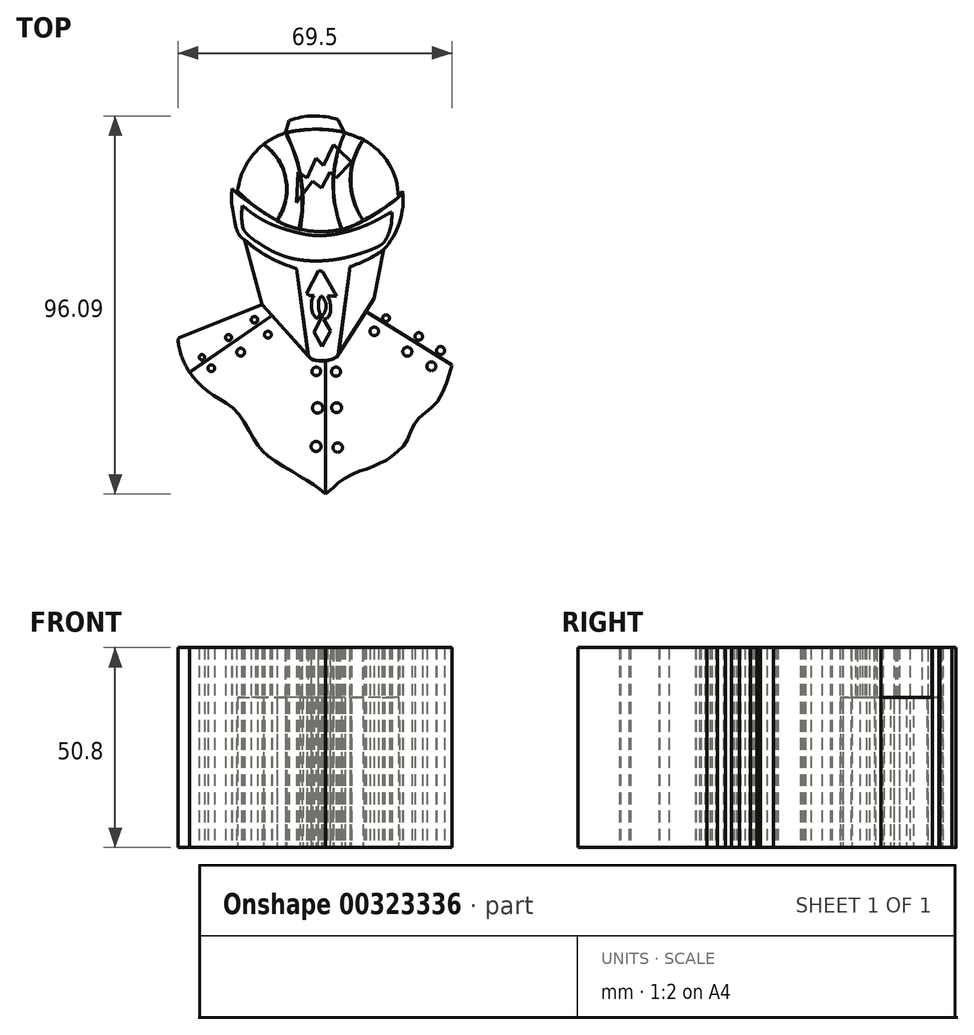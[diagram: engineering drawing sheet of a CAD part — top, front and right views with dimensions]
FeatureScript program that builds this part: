
annotation { "Feature Type Name" : "Feature", "Feature Type Description" : "" }
export const myFeature = defineFeature(function(context is Context, id is Id, definition is map)
    precondition{}
    {
        {
            var Q0;
            Q0=qCreatedBy(makeId("Top.planeOp"),FACE);
            var sketch = newSketch(context, id + "F0", { "sketchPlane" : qUnion([Q0])});
            skPoint(sketch, "E0.5.internal.snap0", {"position": v(-38.58, -5) * mm});
            skFitSpline(sketch, "E1", {"points": [v(3.17, 49.2) * mm, v(3.17, 51.38) * mm, v(4.36, 53.77) * mm, v(5.58, 55.28) * mm, v(6.4, 55.6) * mm], "startDerivative": vector(-2.78, 8.13) * mm, "endDerivative": vector(5, 0.24) * mm});
            skFitSpline(sketch, "E2", {"points": [v(6.4, 55.6) * mm, v(5.5, 55.6) * mm, v(4.17, 55.36) * mm, v(3.1, 54.85) * mm], "startDerivative": vector(-2.76, 0.02) * mm, "endDerivative": vector(-2.66, -2.04) * mm});
            skFitSpline(sketch, "E3", {"points": [v(-37.42, -15.23) * mm, v(-40.07, -14.45) * mm, v(-42.59, -12.85) * mm, v(-44.95, -10.57) * mm, v(-45.68, -9.23) * mm], "startDerivative": vector(-6.72, 1.71) * mm, "endDerivative": vector(-3.89, 6.91) * mm});
            skFitSpline(sketch, "E4", {"points": [v(-33.85, -21.35) * mm, v(-35.18, -21.04) * mm, v(-36.77, -20.04) * mm, v(-38.7, -18.56) * mm, v(-40.23, -17.3) * mm, v(-41.82, -15.67) * mm, v(-43.02, -14.15) * mm, v(-44.07, -12.6) * mm, v(-44.95, -10.57) * mm], "startDerivative": vector(-12.19, 3.35) * mm, "endDerivative": vector(-3.92, 14.92) * mm});
            skFitSpline(sketch, "E5", {"points": [v(-33.85, -21.35) * mm, v(-36.77, -21.35) * mm, v(-41.14, -20.04) * mm, v(-44.91, -17.58) * mm, v(-48.05, -15.2) * mm, v(-51.02, -12.7) * mm, v(-51.87, -11.77) * mm], "startDerivative": vector(-19.18, -1.77) * mm, "endDerivative": vector(-6.72, 8.19) * mm});
            skFitSpline(sketch, "E6", {"points": [v(-45.37, -22.95) * mm, v(-47.5, -20.4) * mm, v(-49.36, -17.7) * mm, v(-50.97, -14.47) * mm, v(-51.64, -12.05) * mm], "startDerivative": vector(-8.52, 9.89) * mm, "endDerivative": vector(-2.33, 10.48) * mm});
            skFitSpline(sketch, "E7", {"points": [v(-45.37, -22.95) * mm, v(-47.83, -21.76) * mm, v(-50.88, -19.05) * mm, v(-53.77, -16.25) * mm, v(-56.9, -10.9) * mm, v(-59.87, -3.61) * mm, v(-60.21, 1.3) * mm, v(-60.08, 8.22) * mm, v(-58.87, 16.53) * mm, v(-56.99, 22.54) * mm], "startDerivative": vector(-31.26, 11.84) * mm, "endDerivative": vector(15.62, 44.98) * mm});
            skFitSpline(sketch, "E8", {"points": [v(-56.99, 22.54) * mm, v(-60.02, 19.8) * mm, v(-62.58, 16.04) * mm, v(-64.55, 11.73) * mm, v(-65.36, 9.97) * mm], "startDerivative": vector(-11.94, -9.26) * mm, "endDerivative": vector(-4.08, -8.6) * mm});
            skFitSpline(sketch, "E9", {"points": [v(-65.36, 9.97) * mm, v(-65.36, 13.35) * mm, v(-64.55, 17.3) * mm, v(-61.94, 22) * mm, v(-57.1, 26.82) * mm, v(-50.5, 32.67) * mm, v(-44.02, 37.62) * mm, v(-37.54, 43.35) * mm], "startDerivative": vector(-1.19, 31.85) * mm, "endDerivative": vector(38.6, 34.69) * mm});
            skFitSpline(sketch, "E10", {"points": [v(-37.54, 43.35) * mm, v(-40.71, 43.35) * mm, v(-44.89, 44.21) * mm], "startDerivative": vector(-5.58, -0.44) * mm, "endDerivative": vector(-8.92, 2.74) * mm});
            skFitSpline(sketch, "E11", {"points": [v(-44.89, 44.21) * mm, v(-38.54, 45.62) * mm, v(-33.26, 48.48) * mm, v(-29.16, 52.33) * mm, v(-25.38, 57.68) * mm], "startDerivative": vector(24.45, 4.86) * mm, "endDerivative": vector(14.44, 21.12) * mm});
            skFitSpline(sketch, "E12", {"points": [v(-25.38, 57.68) * mm, v(-27.85, 58.31) * mm, v(-29.51, 59.52) * mm], "startDerivative": vector(-5, 0.84) * mm, "endDerivative": vector(-3.24, 2.88) * mm});
            skPoint(sketch, "E13.1.internal.orphan", {"position": v(-26.56, 59.52) * mm});
            skFitSpline(sketch, "E14", {"points": [v(-29.51, 59.52) * mm, v(-26.56, 59.52) * mm, v(-22.37, 60.82) * mm, v(-18.75, 62.73) * mm, v(-15.23, 64.3) * mm, v(-11.85, 65.15) * mm, v(-7.52, 65.1) * mm, v(-4.66, 64.25) * mm, v(-1.43, 62.63) * mm, v(1, 60.35) * mm, v(2.48, 58.2) * mm], "startDerivative": vector(30.79, -2.41) * mm, "endDerivative": vector(15.16, -26.8) * mm});
            skLineSegment(sketch, "E15", {"start": v(2.48, 58.2) * mm, "end": v(4, 58.2) * mm});
            skFitSpline(sketch, "E16", {"points": [v(3.1, 54.85) * mm, v(2.83, 56.16) * mm, v(2.75, 56.88) * mm, v(4, 58.2) * mm], "startDerivative": vector(-1.43, 4.3) * mm, "endDerivative": vector(4.07, 3.36) * mm});
            skFitSpline(sketch, "E17", {"points": [v(-40.8, -9.23) * mm, v(-37.42, -15.23) * mm], "startDerivative": vector(2.46, -5.77) * mm, "endDerivative": vector(4.1, -5.12) * mm});
            skFitSpline(sketch, "E18", {"points": [v(-40.8, -9.23) * mm, v(-41.34, -6.01) * mm, v(-40.32, 0.72) * mm, v(-38.3, 6) * mm, v(-36.65, 9.18) * mm, v(-34.54, 11.83) * mm, v(-33.45, 8.56) * mm, v(-33.17, 6.34) * mm, v(-33.07, 3.77) * mm, v(-33.78, 1.02) * mm, v(-34.45, -0.4) * mm, v(-32.03, 3.58) * mm, v(-29.78, 9.89) * mm, v(-29.24, 14.78) * mm, v(-29.7, 21) * mm, v(-22.03, 15.86) * mm], "startDerivative": vector(-12.69, 50.04) * mm, "endDerivative": vector(251.15, -17.71) * mm});
            skFitSpline(sketch, "E19", {"points": [v(-29.7, 21) * mm, v(-27.95, 19.19) * mm, v(-26.25, 18.41) * mm], "startDerivative": vector(2.7, -3.56) * mm, "endDerivative": vector(4.61, -1.7) * mm});
            skFitSpline(sketch, "E20", {"points": [v(-26.25, 18.41) * mm, v(-27.43, 22.43) * mm, v(-26.48, 32.24) * mm, v(-21.58, 41.5) * mm, v(-18.1, 45.6) * mm], "startDerivative": vector(-10.1, 14.02) * mm, "endDerivative": vector(16.54, 18.07) * mm});
            skFitSpline(sketch, "E21", {"points": [v(-18.1, 45.6) * mm, v(-17.52, 44.4) * mm, v(-16.45, 43.21) * mm], "startDerivative": vector(1.01, -2.54) * mm, "endDerivative": vector(2.27, -2.22) * mm});
            skFitSpline(sketch, "E22", {"points": [v(-16.45, 43.21) * mm, v(-14, 49.79) * mm, v(-12.38, 50.2) * mm, v(-10.77, 49.85) * mm, v(-9.1, 49.13) * mm], "startDerivative": vector(-0.26, 17.48) * mm, "endDerivative": vector(9.52, -3.93) * mm});
            skArc(sketch, "E23", {"start": v(3.17, 49.2) * mm, "mid": v(-2.97, 50.24) * mm, "end": v(-9.1, 49.13) * mm});
            skSolve(sketch);
        }
        {
            var Q0;
            Q0=qCreatedBy(makeId("Top.planeOp"),FACE);
            var sketch = newSketch(context, id + "F1", { "sketchPlane" : qUnion([Q0])});
            skLineSegment(sketch, "E24", {"start": v(2.02, 42.8) * mm, "end": v(6.56, 38.46) * mm});
            skLineSegment(sketch, "E25", {"start": v(6.56, 38.46) * mm, "end": v(2.61, 34.34) * mm});
            skLineSegment(sketch, "E26", {"start": v(2.61, 34.34) * mm, "end": v(1.07, 35.81) * mm});
            skLineSegment(sketch, "E27", {"start": v(1.07, 35.81) * mm, "end": v(-1.03, 31.83) * mm});
            skLineSegment(sketch, "E28", {"start": v(-1.03, 31.83) * mm, "end": v(-3.27, 33.53) * mm});
            skLineSegment(sketch, "E29", {"start": v(-3.27, 33.53) * mm, "end": v(-7.36, 28.12) * mm});
            skLineSegment(sketch, "E30", {"start": v(-7.36, 28.12) * mm, "end": v(-7.05, 35.81) * mm});
            skLineSegment(sketch, "E31", {"start": v(-7.05, 35.81) * mm, "end": v(-4.67, 34.34) * mm});
            skLineSegment(sketch, "E32", {"start": v(-4.67, 34.34) * mm, "end": v(-2.43, 39.38) * mm});
            skLineSegment(sketch, "E33", {"start": v(-2.43, 39.38) * mm, "end": v(-0.52, 37.52) * mm});
            skLineSegment(sketch, "E34", {"start": v(-0.52, 37.52) * mm, "end": v(2.02, 42.8) * mm});
            skSolve(sketch);
        }
        {
            var Q0;
            Q0=qCreatedBy(makeId("Top.planeOp"),FACE);
            var sketch = newSketch(context, id + "F2", { "sketchPlane" : qUnion([Q0])});
            skArc(sketch, "E35", {"start": v(3.2, 49.16) * mm, "mid": v(-3.09, 50.14) * mm, "end": v(-9.34, 48.94) * mm});
            skArc(sketch, "E36", {"start": v(4.63, 46.02) * mm, "mid": v(-2.8, 46.76) * mm, "end": v(-10.2, 45.74) * mm});
            skLineSegment(sketch, "E37", {"start": v(-9.34, 48.94) * mm, "end": v(-10.2, 45.74) * mm});
            skLineSegment(sketch, "E38", {"start": v(3.2, 49.16) * mm, "end": v(4.63, 46.02) * mm});
            skSolve(sketch);
        }
        {
            var Q0;
            Q0=qCreatedBy(makeId("Top.planeOp"),FACE);
            var sketch = newSketch(context, id + "F3", { "sketchPlane" : qUnion([Q0])});
            skCircle(sketch, "E39", {"center": v(-18.08, -1.66) * mm, "radius": 0.83 * mm});
            skCircle(sketch, "E40", {"center": v(-24.68, -6.15) * mm, "radius": 0.76 * mm});
            skCircle(sketch, "E41", {"center": v(-31.42, -11.18) * mm, "radius": 0.68 * mm});
            skCircle(sketch, "E42", {"center": v(-14.66, -5.43) * mm, "radius": 0.86 * mm});
            skCircle(sketch, "E43", {"center": v(-21.58, -9.88) * mm, "radius": 1 * mm});
            skCircle(sketch, "E44", {"center": v(-29.05, -13.98) * mm, "radius": 0.85 * mm});
            skCircle(sketch, "E45", {"center": v(-2.39, -14.77) * mm, "radius": 1.1 * mm});
            skCircle(sketch, "E46", {"center": v(2.63, -14.83) * mm, "radius": 1.16 * mm});
            skCircle(sketch, "E47", {"center": v(2.79, -24) * mm, "radius": 1.25 * mm});
            skCircle(sketch, "E48", {"center": v(-2.02, -24.05) * mm, "radius": 1.32 * mm});
            skCircle(sketch, "E49", {"center": v(3.07, -34.12) * mm, "radius": 1.19 * mm});
            skCircle(sketch, "E50", {"center": v(-2.42, -33.84) * mm, "radius": 1.26 * mm});
            skCircle(sketch, "E51", {"center": v(15.35, -1.23) * mm, "radius": 0.85 * mm});
            skCircle(sketch, "E52", {"center": v(12.35, -4.6) * mm, "radius": 1.08 * mm});
            skCircle(sketch, "E53", {"center": v(20.75, -9.75) * mm, "radius": 1.15 * mm});
            skCircle(sketch, "E54", {"center": v(23.64, -5.89) * mm, "radius": 0.97 * mm});
            skCircle(sketch, "E55", {"center": v(29.21, -9.48) * mm, "radius": 1.03 * mm});
            skCircle(sketch, "E56", {"center": v(26.86, -13.47) * mm, "radius": 1.14 * mm});
            skSolve(sketch);
        }
        {
            var Q0;
            Q0=qCreatedBy(makeId("Top.planeOp"),FACE);
            var sketch = newSketch(context, id + "F4", { "sketchPlane" : qUnion([Q0])});
            skLineSegment(sketch, "E57", {"start": v(-13.65, -0.62) * mm, "end": v(-34.52, -15.07) * mm});
            skFitSpline(sketch, "E58", {"points": [v(-34.52, -15.07) * mm, v(-35.36, -13.64) * mm, v(-36.64, -10.74) * mm, v(-37.45, -7.24) * mm, v(-37.41, -6.27) * mm], "startDerivative": vector(-4.3, 5.95) * mm, "endDerivative": vector(-0.06, 5.27) * mm});
            skLineSegment(sketch, "E59", {"start": v(-37.41, -6.27) * mm, "end": v(-16.17, 2.17) * mm});
            skLineSegment(sketch, "E60", {"start": v(-16.17, 2.17) * mm, "end": v(-13.65, -0.62) * mm});
            skSolve(sketch);
        }
        {
            var Q0;
            Q0=qCreatedBy(makeId("Top.planeOp"),FACE);
            var sketch = newSketch(context, id + "F5", { "sketchPlane" : qUnion([Q0])});
            skLineSegment(sketch, "E61", {"start": v(0, -11.98) * mm, "end": v(0, -45.87) * mm});
            skFitSpline(sketch, "E62", {"points": [v(0, -45.87) * mm, v(-3.53, -43.21) * mm, v(-7.53, -40.79) * mm, v(-13.74, -36.9) * mm, v(-16.76, -34.13) * mm, v(-19.58, -29.6) * mm, v(-23.2, -24.33) * mm, v(-27.17, -21.71) * mm, v(-29.93, -19.85) * mm, v(-32.81, -17.22) * mm, v(-34.6, -14.93) * mm], "startDerivative": vector(-33.38, 29.98) * mm, "endDerivative": vector(-20.83, 28.91) * mm});
            skLineSegment(sketch, "E63", {"start": v(-34.6, -14.93) * mm, "end": v(-13.63, -0.58) * mm});
            skLineSegment(sketch, "E64", {"start": v(-13.63, -0.58) * mm, "end": v(-4.48, -10.88) * mm});
            skFitSpline(sketch, "E65", {"points": [v(0, -11.98) * mm, v(-2.15, -11.98) * mm, v(-4.48, -10.88) * mm], "startDerivative": vector(-4.76, -0.54) * mm, "endDerivative": vector(-5.48, 6.35) * mm});
            skSolve(sketch);
        }
        {
            var Q0;
            Q0=qCreatedBy(makeId("Top.planeOp"),FACE);
            var sketch = newSketch(context, id + "F6", { "sketchPlane" : qUnion([Q0])});
            skFitSpline(sketch, "E66", {"points": [v(0, -12.02) * mm, v(1.67, -11.65) * mm, v(3.12, -10.57) * mm], "startDerivative": vector(3.05, 0.5) * mm, "endDerivative": vector(2.8, 3.5) * mm});
            skLineSegment(sketch, "E67", {"start": v(10.25, 0.49) * mm, "end": v(3.12, -10.57) * mm});
            skLineSegment(sketch, "E68", {"start": v(10.25, 0.49) * mm, "end": v(32.05, -13.15) * mm});
            skFitSpline(sketch, "E69", {"points": [v(32.05, -13.15) * mm, v(30.86, -17.4) * mm, v(28.41, -22.3) * mm, v(26.03, -24.64) * mm, v(23.24, -27.05) * mm, v(21.56, -30.15) * mm, v(20.24, -33.16) * mm, v(17.93, -35.4) * mm, v(15.82, -37.17) * mm, v(13.87, -38.01) * mm, v(11.52, -39.2) * mm, v(8.59, -40.09) * mm, v(5.42, -41.64) * mm, v(2.85, -43.43) * mm, v(0, -45.95) * mm], "startDerivative": vector(-12.39, -50.75) * mm, "endDerivative": vector(-67.42, -50.47) * mm});
            skLineSegment(sketch, "E70", {"start": v(0, -12.02) * mm, "end": v(0, -45.95) * mm});
            skSolve(sketch);
        }
        {
            var Q0;
            Q0=qCreatedBy(makeId("Top.planeOp"),FACE);
            var sketch = newSketch(context, id + "F7", { "sketchPlane" : qUnion([Q0])});
            skArc(sketch, "E71", {"start": v(-6.74, 21.44) * mm, "mid": v(-6.29, 33.96) * mm, "end": v(-10.23, 45.85) * mm});
            skArc(sketch, "E72", {"start": v(-12.4, 23.46) * mm, "mid": v(-10, 33.9) * mm, "end": v(-15.74, 42.95) * mm});
            skArc(sketch, "E73", {"start": v(4.93, 45.83) * mm, "mid": v(1.9, 33.67) * mm, "end": v(4.18, 21.35) * mm});
            skArc(sketch, "E74", {"start": v(9.71, 44.09) * mm, "mid": v(6.42, 33.93) * mm, "end": v(9.53, 23.71) * mm});
            skArc(sketch, "E75", {"start": v(-10.23, 45.85) * mm, "mid": v(-13.1, 44.6) * mm, "end": v(-15.74, 42.95) * mm});
            skArc(sketch, "E76", {"start": v(9.71, 44.09) * mm, "mid": v(7.34, 45.02) * mm, "end": v(4.93, 45.83) * mm});
            skArc(sketch, "E77", {"start": v(4.18, 21.35) * mm, "mid": v(6.97, 22.27) * mm, "end": v(9.53, 23.71) * mm});
            skArc(sketch, "E78", {"start": v(-12.4, 23.46) * mm, "mid": v(-9.65, 22.22) * mm, "end": v(-6.74, 21.44) * mm});
            skSolve(sketch);
        }
        {
            var Q0;
            Q0=qCreatedBy(makeId("Top.planeOp"),FACE);
            var sketch = newSketch(context, id + "F8", { "sketchPlane" : qUnion([Q0])});
            skArc(sketch, "E79", {"start": v(-15.83, 42.88) * mm, "mid": v(-20.24, 37.64) * mm, "end": v(-22.33, 31.12) * mm});
            skArc(sketch, "E80", {"start": v(-12.48, 23.57) * mm, "mid": v(-10.1, 33.93) * mm, "end": v(-15.83, 42.88) * mm});
            skArc(sketch, "E81", {"start": v(18.5, 29.42) * mm, "mid": v(16.04, 38) * mm, "end": v(9.54, 44.1) * mm});
            skArc(sketch, "E82", {"start": v(9.54, 44.1) * mm, "mid": v(6.26, 33.89) * mm, "end": v(9.54, 23.67) * mm});
            skArc(sketch, "E83", {"start": v(4.89, 45.95) * mm, "mid": v(-2.64, 46.74) * mm, "end": v(-10.16, 45.9) * mm});
            skArc(sketch, "E84", {"start": v(-6.5, 21.37) * mm, "mid": v(-1.23, 20.76) * mm, "end": v(4.03, 21.36) * mm});
            skArc(sketch, "E85", {"start": v(-6.5, 21.37) * mm, "mid": v(-6.18, 33.96) * mm, "end": v(-10.16, 45.9) * mm});
            skArc(sketch, "E86", {"start": v(4.89, 45.95) * mm, "mid": v(2.03, 33.74) * mm, "end": v(4.03, 21.36) * mm});
            skArc(sketch, "E87", {"start": v(-22.33, 31.12) * mm, "mid": v(-15.08, 25.17) * mm, "end": v(-6.5, 21.37) * mm});
            skArc(sketch, "E88", {"start": v(4.03, 21.36) * mm, "mid": v(11.62, 24.77) * mm, "end": v(18.5, 29.42) * mm});
            skSolve(sketch);
        }
        {
            var Q0;
            Q0=qCreatedBy(makeId("Top.planeOp"),FACE);
            var sketch = newSketch(context, id + "F9", { "sketchPlane" : qUnion([Q0])});
            skArc(sketch, "E89", {"start": v(-21.13, 27.37) * mm, "mid": v(-21.33, 24.32) * mm, "end": v(-20.88, 21.3) * mm});
            skArc(sketch, "E90", {"start": v(14.98, 18.18) * mm, "mid": v(16.5, 21.82) * mm, "end": v(16.78, 25.75) * mm});
            skFitSpline(sketch, "E91", {"points": [v(-21.13, 27.37) * mm, v(-15.56, 23.46) * mm, v(-8.4, 20.81) * mm, v(-1.6, 19.72) * mm, v(6.54, 21.05) * mm, v(12.63, 23.47) * mm, v(16.78, 25.75) * mm], "startDerivative": vector(27.34, -23.18) * mm, "endDerivative": vector(29.72, 15.87) * mm});
            skFitSpline(sketch, "E92", {"points": [v(-20.88, 21.3) * mm, v(-16.97, 17.82) * mm, v(-13.58, 15.8) * mm, v(-8.54, 13.95) * mm, v(-1.83, 13.3) * mm, v(4.82, 14.09) * mm, v(10.16, 15.66) * mm, v(14.98, 18.18) * mm], "startDerivative": vector(25.85, -38.76) * mm, "endDerivative": vector(21.97, 24.9) * mm});
            skLineSegment(sketch, "E93", {"start": v(15.4, 25.01) * mm, "end": v(14.98, 18.18) * mm});
            skLineSegment(sketch, "E94", {"start": v(14.18, 24.3) * mm, "end": v(13.75, 17.19) * mm});
            skLineSegment(sketch, "E95", {"start": v(12.63, 23.47) * mm, "end": v(12.43, 16.52) * mm});
            skLineSegment(sketch, "E96", {"start": v(11.06, 22.72) * mm, "end": v(11.06, 15.97) * mm});
            skLineSegment(sketch, "E97", {"start": v(9.5, 22.07) * mm, "end": v(9.36, 15.44) * mm});
            skLineSegment(sketch, "E98", {"start": v(8.23, 21.6) * mm, "end": v(7.82, 14.88) * mm});
            skLineSegment(sketch, "E99", {"start": v(6.54, 21.05) * mm, "end": v(6.44, 14.48) * mm});
            skLineSegment(sketch, "E100", {"start": v(5.1, 20.65) * mm, "end": v(4.82, 14.09) * mm});
            skLineSegment(sketch, "E101", {"start": v(3.16, 20.22) * mm, "end": v(3.16, 13.77) * mm});
            skLineSegment(sketch, "E102", {"start": v(1.56, 19.95) * mm, "end": v(1.56, 13.53) * mm});
            skLineSegment(sketch, "E103", {"start": v(0, 19.78) * mm, "end": v(0.3, 13.4) * mm});
            skLineSegment(sketch, "E104", {"start": v(-1.6, 19.72) * mm, "end": v(-1.29, 13.3) * mm});
            skLineSegment(sketch, "E105", {"start": v(-3.22, 19.8) * mm, "end": v(-2.98, 13.3) * mm});
            skLineSegment(sketch, "E106", {"start": v(-5, 20.03) * mm, "end": v(-4.65, 13.36) * mm});
            skLineSegment(sketch, "E107", {"start": v(-6.58, 20.35) * mm, "end": v(-6.11, 13.51) * mm});
            skLineSegment(sketch, "E108", {"start": v(-7.87, 20.67) * mm, "end": v(-7.87, 13.8) * mm});
            skLineSegment(sketch, "E109", {"start": v(-9.53, 21.13) * mm, "end": v(-9.53, 14.2) * mm});
            skLineSegment(sketch, "E110", {"start": v(-11.47, 21.74) * mm, "end": v(-11.47, 14.86) * mm});
            skLineSegment(sketch, "E111", {"start": v(-13.13, 22.34) * mm, "end": v(-13.13, 15.57) * mm});
            skLineSegment(sketch, "E112", {"start": v(-14.88, 23.11) * mm, "end": v(-14.88, 16.51) * mm});
            skLineSegment(sketch, "E113", {"start": v(-16.22, 23.82) * mm, "end": v(-16.17, 17.31) * mm});
            skLineSegment(sketch, "E114", {"start": v(-17.93, 24.9) * mm, "end": v(-17.93, 18.44) * mm});
            skLineSegment(sketch, "E115", {"start": v(-19.25, 25.86) * mm, "end": v(-19.25, 19.44) * mm});
            skLineSegment(sketch, "E116", {"start": v(-20.21, 26.61) * mm, "end": v(-20.21, 20.42) * mm});
            skSolve(sketch);
        }
        {
            var Q0;
            Q0=qCreatedBy(makeId("Top.planeOp"),FACE);
            var sketch = newSketch(context, id + "F10", { "sketchPlane" : qUnion([Q0])});
            skLineSegment(sketch, "E117", {"start": v(-0.82, 8.75) * mm, "end": v(-2.66, 5.06) * mm});
            skLineSegment(sketch, "E118", {"start": v(-1.14, 8.1) * mm, "end": v(0.9, 4.95) * mm});
            skLineSegment(sketch, "E119", {"start": v(0.9, 4.95) * mm, "end": v(1.66, 4.95) * mm});
            skLineSegment(sketch, "E120", {"start": v(1.66, 4.95) * mm, "end": v(-0.82, 8.75) * mm});
            skLineSegment(sketch, "E121", {"start": v(-0.78, 10.66) * mm, "end": v(-3.96, 4.48) * mm});
            skLineSegment(sketch, "E122", {"start": v(-3.96, 4.48) * mm, "end": v(-4.87, 4.95) * mm});
            skLineSegment(sketch, "E123", {"start": v(-4.87, 4.95) * mm, "end": v(-1.82, 10.87) * mm});
            skLineSegment(sketch, "E124", {"start": v(-1.82, 10.87) * mm, "end": v(-0.78, 10.66) * mm});
            skLineSegment(sketch, "E125", {"start": v(-0.78, 10.66) * mm, "end": v(2.79, 4.42) * mm});
            skLineSegment(sketch, "E126", {"start": v(2.79, 4.42) * mm, "end": v(-1.07, 4.42) * mm});
            skLineSegment(sketch, "E127", {"start": v(0.9, 4.95) * mm, "end": v(-0.7, 4.95) * mm});
            skArc(sketch, "E128", {"start": v(-0.7, 4.95) * mm, "mid": v(-1.03, 4.78) * mm, "end": v(-1.07, 4.42) * mm});
            skLineSegment(sketch, "E129", {"start": v(-3.96, 4.48) * mm, "end": v(-2.78, 4.48) * mm});
            skFitSpline(sketch, "E130", {"points": [v(-2.66, 5.06) * mm, v(-2.78, 4.48) * mm], "startDerivative": vector(-0.29, -0.57) * mm, "endDerivative": vector(-0.29, -0.57) * mm});
            skLineSegment(sketch, "E131", {"start": v(-0.89, -2.1) * mm, "end": v(-1.22, -2.74) * mm});
            skLineSegment(sketch, "E132", {"start": v(-1.22, -2.74) * mm, "end": v(-0.26, -4.33) * mm});
            skLineSegment(sketch, "E133", {"start": v(-0.26, -4.33) * mm, "end": v(-1.13, -6.24) * mm});
            skLineSegment(sketch, "E134", {"start": v(-1.13, -6.24) * mm, "end": v(-0.83, -6.66) * mm});
            skLineSegment(sketch, "E135", {"start": v(-0.83, -6.66) * mm, "end": v(0.52, -4.44) * mm});
            skLineSegment(sketch, "E136", {"start": v(0.52, -4.44) * mm, "end": v(-0.89, -2.1) * mm});
            skLineSegment(sketch, "E137", {"start": v(-1.22, -2.74) * mm, "end": v(-2.2, -4.56) * mm});
            skLineSegment(sketch, "E138", {"start": v(-2.2, -4.56) * mm, "end": v(-1.13, -6.24) * mm});
            skLineSegment(sketch, "E139", {"start": v(-0.89, -8.5) * mm, "end": v(-1.83, -8.5) * mm});
            skLineSegment(sketch, "E140", {"start": v(-1.83, -8.5) * mm, "end": v(-3.82, -4.68) * mm});
            skLineSegment(sketch, "E141", {"start": v(-3.82, -4.68) * mm, "end": v(-1.4, -0.23) * mm});
            skLineSegment(sketch, "E142", {"start": v(-0.86, -8.5) * mm, "end": v(1.23, -4.56) * mm});
            skLineSegment(sketch, "E143", {"start": v(1.23, -4.56) * mm, "end": v(-0.55, -1.5) * mm});
            skLineSegment(sketch, "E144", {"start": v(-0.85, -0.58) * mm, "end": v(-2.96, -4.72) * mm});
            skLineSegment(sketch, "E145", {"start": v(-2.96, -4.72) * mm, "end": v(-0.86, -8.5) * mm});
            skFitSpline(sketch, "E146", {"points": [v(-1.07, 4.42) * mm, v(-1.47, 3.93) * mm, v(-1.85, 1.88) * mm, v(-1.4, -0.23) * mm], "startDerivative": vector(-1.7, -2.56) * mm, "endDerivative": vector(1.57, -4.12) * mm});
            skLineSegment(sketch, "E147", {"start": v(-1.07, 4.42) * mm, "end": v(-1.07, 4.42) * mm});
            skArc(sketch, "E148", {"start": v(-0.85, -0.58) * mm, "mid": v(0.12, 1.97) * mm, "end": v(-1.07, 4.42) * mm});
            skPoint(sketch, "E149.4.internal.snap0", {"position": v(0.1, 4.95) * mm});
            skFitSpline(sketch, "E149", {"points": [v(0.37, 4.95) * mm, v(0, 5.56) * mm, v(-0.63, 5.77) * mm, v(-1.12, 5.67) * mm, v(-1.81, 4.95) * mm, v(-2.21, 4.14) * mm, v(-2.58, 2.48) * mm, v(-2.58, 1.4) * mm, v(-2.33, -0.16) * mm, v(-1.7, -0.79) * mm], "startDerivative": vector(-3.05, 7.16) * mm, "endDerivative": vector(7.6, -4.23) * mm});
            skFitSpline(sketch, "E150", {"points": [v(-1.98, -1.31) * mm, v(-2.76, -0.8) * mm, v(-3.34, 0.31) * mm, v(-3.54, 1.2) * mm, v(-3.57, 2.9) * mm, v(-3.3, 3.87) * mm, v(-2.98, 4.48) * mm], "startDerivative": vector(-5.25, 2.49) * mm, "endDerivative": vector(2.35, 4.37) * mm});
            skFitSpline(sketch, "E151", {"points": [v(-0.35, 4.42) * mm, v(0, 3.96) * mm, v(0.48, 2.83) * mm, v(0.66, 1.23) * mm, v(0.44, 0.22) * mm, v(0, -0.24) * mm, v(-0.7, -0.43) * mm], "startDerivative": vector(3.9, -3.78) * mm, "endDerivative": vector(-6.95, -0.81) * mm});
            skFitSpline(sketch, "E152", {"points": [v(0.5, 4.42) * mm, v(1.03, 3.28) * mm, v(1.17, 2.36) * mm, v(1.21, 0.53) * mm, v(0.72, -0.9) * mm, v(0, -1.4) * mm, v(-0.55, -1.5) * mm], "startDerivative": vector(2.71, -5.1) * mm, "endDerivative": vector(-2.95, -1.84) * mm});
            skLineSegment(sketch, "E153", {"start": v(-0.55, -1.5) * mm, "end": v(-0.7, -0.43) * mm});
            skSolve(sketch);
        }
        {
            var Q0;
            Q0=qCreatedBy(makeId("Top.planeOp"),FACE);
            var sketch = newSketch(context, id + "F11", { "sketchPlane" : qUnion([Q0])});
            skLineSegment(sketch, "E154", {"start": v(-20.58, 18.68) * mm, "end": v(-16.18, 2.18) * mm});
            skLineSegment(sketch, "E155", {"start": v(-16.18, 2.18) * mm, "end": v(-4.5, -10.77) * mm});
            skLineSegment(sketch, "E156", {"start": v(-4.5, -10.77) * mm, "end": v(-7.33, 11.39) * mm});
            skArc(sketch, "E157", {"start": v(-20.58, 18.68) * mm, "mid": v(-14.38, 14.27) * mm, "end": v(-7.33, 11.39) * mm});
            skFitSpline(sketch, "E158", {"points": [v(-4.5, -10.77) * mm, v(-2.16, -11.97) * mm, v(0, -12) * mm, v(1.73, -11.61) * mm, v(3.13, -10.6) * mm], "startDerivative": vector(10.13, -13.34) * mm, "endDerivative": vector(4.96, 7.31) * mm});
            skLineSegment(sketch, "E159", {"start": v(6.24, 11.85) * mm, "end": v(3.13, -10.6) * mm});
            skLineSegment(sketch, "E160", {"start": v(3.13, -10.6) * mm, "end": v(12.32, 3.71) * mm});
            skLineSegment(sketch, "E161", {"start": v(12.32, 3.71) * mm, "end": v(14.64, 16.1) * mm});
            skArc(sketch, "E162", {"start": v(6.24, 11.85) * mm, "mid": v(10.59, 13.68) * mm, "end": v(14.64, 16.1) * mm});
            skSolve(sketch);
        }
        {
            var Q0;
            Q0=qCreatedBy(makeId("Top.planeOp"),FACE);
            var sketch = newSketch(context, id + "F12", { "sketchPlane" : qUnion([Q0])});
            skFitSpline(sketch, "E163", {"points": [v(-23.75, 31.62) * mm, v(-23.86, 28.1) * mm, v(-23, 22.89) * mm, v(-22.05, 20.01) * mm, v(-20.55, 18.52) * mm], "startDerivative": vector(-1.16, -12.85) * mm, "endDerivative": vector(8.4, -6.75) * mm});
            skArc(sketch, "E164", {"start": v(-20.55, 18.52) * mm, "mid": v(-14.35, 14.23) * mm, "end": v(-7.35, 11.39) * mm});
            skLineSegment(sketch, "E165", {"start": v(-7.35, 11.39) * mm, "end": v(-4.32, -10.84) * mm});
            skFitSpline(sketch, "E166", {"points": [v(-23.75, 31.62) * mm, v(-22.59, 30.53) * mm, v(-12.42, 23.56) * mm, v(-6.77, 21.38) * mm, v(4.3, 21.29) * mm, v(18.76, 29.67) * mm], "startDerivative": vector(8.62, -9.5) * mm, "endDerivative": vector(47.11, 35.88) * mm});
            skLineSegment(sketch, "E167", {"start": v(19.58, 31.03) * mm, "end": v(18.76, 29.67) * mm});
            skFitSpline(sketch, "E168", {"points": [v(-4.32, -10.84) * mm, v(-2.09, -12.01) * mm, v(0, -12.08) * mm, v(1.67, -11.68) * mm, v(3.21, -10.84) * mm], "startDerivative": vector(3.83, -8.2) * mm, "endDerivative": vector(19.81, 10.72) * mm});
            skLineSegment(sketch, "E169", {"start": v(3.21, -10.84) * mm, "end": v(6.23, 11.86) * mm});
            skArc(sketch, "E170", {"start": v(6.23, 11.86) * mm, "mid": v(10.59, 13.63) * mm, "end": v(14.62, 16.05) * mm});
            skArc(sketch, "E171", {"start": v(14.62, 16.05) * mm, "mid": v(18.75, 23) * mm, "end": v(19.58, 31.03) * mm});
            skSolve(sketch);
        }
        {
            var Q0;
            {var subQ0=sQuery(id+"F9.wireOp",EDGE,"E105");Q0=makeQuery(id+"F9.imprint","IMPRINT",FACE,{"disambiguationData":[TD([[makeQuery(id+"F9.imprint","IMPRINT",EDGE,{"derivedFrom":subQ0}),-1.0]])]});}
            var Q1;
            Q1=makeQuery(id+"F8.imprint","IMPRINT",FACE,{"disambiguationData":[TD([[makeQuery(id+"F8.imprint","IMPRINT",EDGE,{"derivedFrom":sQuery(id+"F8.wireOp",EDGE,"E83")}),1.0]])]});
            var Q2;
            {var subQ0=sQuery(id+"F8.wireOp",EDGE,"E81");Q2=makeQuery(id+"F8.imprint","IMPRINT",FACE,{"disambiguationData":[TD([[makeQuery(id+"F8.imprint","IMPRINT",EDGE,{"derivedFrom":subQ0}),1.0]])]});}
            var Q3;
            {var subQ0=sQuery(id+"F8.wireOp",EDGE,"E79");Q3=makeQuery(id+"F8.imprint","IMPRINT",FACE,{"disambiguationData":[TD([[makeQuery(id+"F8.imprint","IMPRINT",EDGE,{"derivedFrom":subQ0}),1.0]])]});}
            var Q4;
            Q4=makeQuery(id+"F7.imprint","IMPRINT",FACE,{"disambiguationData":[TD([[makeQuery(id+"F7.imprint","IMPRINT",EDGE,{"derivedFrom":sQuery(id+"F7.wireOp",EDGE,"E73")}),1.0]])]});
            var Q5;
            Q5=makeQuery(id+"F7.imprint","IMPRINT",FACE,{"disambiguationData":[TD([[makeQuery(id+"F7.imprint","IMPRINT",EDGE,{"derivedFrom":sQuery(id+"F7.wireOp",EDGE,"E71")}),1.0]])]});
            var Q6;
            {var subQ0=sQuery(id+"F9.wireOp",EDGE,"E106");Q6=makeQuery(id+"F9.imprint","IMPRINT",FACE,{"disambiguationData":[TD([[makeQuery(id+"F9.imprint","IMPRINT",EDGE,{"derivedFrom":subQ0}),-1.0]])]});}
            var Q7;
            {var subQ0=sQuery(id+"F9.wireOp",EDGE,"E108");Q7=makeQuery(id+"F9.imprint","IMPRINT",FACE,{"disambiguationData":[TD([[makeQuery(id+"F9.imprint","IMPRINT",EDGE,{"derivedFrom":subQ0}),-1.0]])]});}
            var Q8;
            {var subQ0=sQuery(id+"F9.wireOp",EDGE,"E110");Q8=makeQuery(id+"F9.imprint","IMPRINT",FACE,{"disambiguationData":[TD([[makeQuery(id+"F9.imprint","IMPRINT",EDGE,{"derivedFrom":subQ0}),-1.0]])]});}
            var Q9;
            Q9=makeQuery(id+"F11.imprint","IMPRINT",FACE,{"disambiguationData":[TD([[makeQuery(id+"F11.imprint","IMPRINT",EDGE,{"derivedFrom":sQuery(id+"F11.wireOp",EDGE,"E159")}),1.0]])]});
            var Q10;
            Q10=makeQuery(id+"F6.imprint","IMPRINT",FACE,{"disambiguationData":[TD([[makeQuery(id+"F6.imprint","IMPRINT",EDGE,{"derivedFrom":sQuery(id+"F6.wireOp",EDGE,"E66")}),-1.0]])]});
            var Q11;
            Q11=makeQuery(id+"F12.imprint","IMPRINT",FACE,{"disambiguationData":[TD([[makeQuery(id+"F12.imprint","IMPRINT",EDGE,{"derivedFrom":sQuery(id+"F12.wireOp",EDGE,"E163")}),1.0]])]});
            var Q12;
            {var subQ0=sQuery(id+"F9.wireOp",EDGE,"E101");Q12=makeQuery(id+"F9.imprint","IMPRINT",FACE,{"disambiguationData":[TD([[makeQuery(id+"F9.imprint","IMPRINT",EDGE,{"derivedFrom":subQ0}),-1.0]])]});}
            var Q13;
            Q13=makeQuery(id+"F11.imprint","IMPRINT",FACE,{"disambiguationData":[TD([[makeQuery(id+"F11.imprint","IMPRINT",EDGE,{"derivedFrom":sQuery(id+"F11.wireOp",EDGE,"E154")}),1.0]])]});
            var Q14;
            Q14=makeQuery(id+"F1.imprint","IMPRINT",FACE,{"disambiguationData":[TD([[makeQuery(id+"F1.imprint","IMPRINT",EDGE,{"derivedFrom":sQuery(id+"F1.wireOp",EDGE,"E24")}),-1.0]])]});
            var Q15;
            Q15=makeQuery(id+"F2.imprint","IMPRINT",FACE,{"disambiguationData":[TD([[makeQuery(id+"F2.imprint","IMPRINT",EDGE,{"derivedFrom":sQuery(id+"F2.wireOp",EDGE,"E35")}),1.0]])]});
            var Q16;
            Q16=makeQuery(id+"F4.imprint","IMPRINT",FACE,{"disambiguationData":[TD([[makeQuery(id+"F4.imprint","IMPRINT",EDGE,{"derivedFrom":sQuery(id+"F4.wireOp",EDGE,"E57")}),-1.0]])]});
            var Q17;
            Q17=makeQuery(id+"F5.imprint","IMPRINT",FACE,{"disambiguationData":[TD([[makeQuery(id+"F5.imprint","IMPRINT",EDGE,{"derivedFrom":sQuery(id+"F5.wireOp",EDGE,"E62")}),-1.0]])]});
            var Q18;
            {var subQ3=sQuery(id+"F9.wireOp",EDGE,"E105");Q18=makeQuery(id+"F9.imprint","IMPRINT",FACE,{"disambiguationData":[TD([[makeQuery(id+"F9.imprint","IMPRINT",EDGE,{"derivedFrom":subQ3}),1.0]])]});}
            var Q19;
            {var subQ0=sQuery(id+"F9.wireOp",EDGE,"E102");Q19=makeQuery(id+"F9.imprint","IMPRINT",FACE,{"disambiguationData":[TD([[makeQuery(id+"F9.imprint","IMPRINT",EDGE,{"derivedFrom":subQ0}),-1.0]])]});}
            var Q20;
            {var subQ0=sQuery(id+"F9.wireOp",EDGE,"E94");Q20=makeQuery(id+"F9.imprint","IMPRINT",FACE,{"disambiguationData":[TD([[makeQuery(id+"F9.imprint","IMPRINT",EDGE,{"derivedFrom":subQ0}),-1.0]])]});}
            var Q21;
            {var subQ0=sQuery(id+"F9.wireOp",EDGE,"E96");Q21=makeQuery(id+"F9.imprint","IMPRINT",FACE,{"disambiguationData":[TD([[makeQuery(id+"F9.imprint","IMPRINT",EDGE,{"derivedFrom":subQ0}),-1.0]])]});}
            var Q22;
            {var subQ0=sQuery(id+"F9.wireOp",EDGE,"E98");Q22=makeQuery(id+"F9.imprint","IMPRINT",FACE,{"disambiguationData":[TD([[makeQuery(id+"F9.imprint","IMPRINT",EDGE,{"derivedFrom":subQ0}),-1.0]])]});}
            var Q23;
            {var subQ0=sQuery(id+"F9.wireOp",EDGE,"E99");Q23=makeQuery(id+"F9.imprint","IMPRINT",FACE,{"disambiguationData":[TD([[makeQuery(id+"F9.imprint","IMPRINT",EDGE,{"derivedFrom":subQ0}),-1.0]])]});}
            var Q24;
            {var subQ0=sQuery(id+"F9.wireOp",EDGE,"E100");Q24=makeQuery(id+"F9.imprint","IMPRINT",FACE,{"disambiguationData":[TD([[makeQuery(id+"F9.imprint","IMPRINT",EDGE,{"derivedFrom":subQ0}),-1.0]])]});}
            var Q25;
            {var subQ0=sQuery(id+"F9.wireOp",EDGE,"E90");Q25=makeQuery(id+"F9.imprint","IMPRINT",FACE,{"disambiguationData":[TD([[makeQuery(id+"F9.imprint","IMPRINT",EDGE,{"derivedFrom":subQ0}),1.0]])]});}
            var Q26;
            {var subQ0=sQuery(id+"F9.wireOp",EDGE,"E112");Q26=makeQuery(id+"F9.imprint","IMPRINT",FACE,{"disambiguationData":[TD([[makeQuery(id+"F9.imprint","IMPRINT",EDGE,{"derivedFrom":subQ0}),-1.0]])]});}
            var Q27;
            {var subQ0=sQuery(id+"F9.wireOp",EDGE,"E113");Q27=makeQuery(id+"F9.imprint","IMPRINT",FACE,{"disambiguationData":[TD([[makeQuery(id+"F9.imprint","IMPRINT",EDGE,{"derivedFrom":subQ0}),-1.0]])]});}
            var Q28;
            {var subQ0=sQuery(id+"F9.wireOp",EDGE,"E107");Q28=makeQuery(id+"F9.imprint","IMPRINT",FACE,{"disambiguationData":[TD([[makeQuery(id+"F9.imprint","IMPRINT",EDGE,{"derivedFrom":subQ0}),-1.0]])]});}
            var Q29;
            {var subQ0=sQuery(id+"F9.wireOp",EDGE,"E109");Q29=makeQuery(id+"F9.imprint","IMPRINT",FACE,{"disambiguationData":[TD([[makeQuery(id+"F9.imprint","IMPRINT",EDGE,{"derivedFrom":subQ0}),-1.0]])]});}
            var Q30;
            Q30=makeQuery(id+"F3.imprint","IMPRINT",FACE,{"disambiguationData":[TD([[makeQuery(id+"F3.imprint","IMPRINT",EDGE,{"derivedFrom":sQuery(id+"F3.wireOp",EDGE,"E53")}),1.0]])]});
            var Q31;
            Q31=makeQuery(id+"F3.imprint","IMPRINT",FACE,{"disambiguationData":[TD([[makeQuery(id+"F3.imprint","IMPRINT",EDGE,{"derivedFrom":sQuery(id+"F3.wireOp",EDGE,"E47")}),1.0]])]});
            var Q32;
            Q32=makeQuery(id+"F3.imprint","IMPRINT",FACE,{"disambiguationData":[TD([[makeQuery(id+"F3.imprint","IMPRINT",EDGE,{"derivedFrom":sQuery(id+"F3.wireOp",EDGE,"E48")}),1.0]])]});
            var Q33;
            Q33=makeQuery(id+"F3.imprint","IMPRINT",FACE,{"disambiguationData":[TD([[makeQuery(id+"F3.imprint","IMPRINT",EDGE,{"derivedFrom":sQuery(id+"F3.wireOp",EDGE,"E56")}),1.0]])]});
            var Q34;
            {var subQ0=sQuery(id+"F9.wireOp",EDGE,"E115");Q34=makeQuery(id+"F9.imprint","IMPRINT",FACE,{"disambiguationData":[TD([[makeQuery(id+"F9.imprint","IMPRINT",EDGE,{"derivedFrom":subQ0}),-1.0]])]});}
            var Q35;
            {var subQ0=sQuery(id+"F9.wireOp",EDGE,"E111");Q35=makeQuery(id+"F9.imprint","IMPRINT",FACE,{"disambiguationData":[TD([[makeQuery(id+"F9.imprint","IMPRINT",EDGE,{"derivedFrom":subQ0}),-1.0]])]});}
            var Q36;
            {var subQ0=sQuery(id+"F9.wireOp",EDGE,"E94");Q36=makeQuery(id+"F9.imprint","IMPRINT",FACE,{"disambiguationData":[TD([[makeQuery(id+"F9.imprint","IMPRINT",EDGE,{"derivedFrom":subQ0}),1.0]])]});}
            var Q37;
            Q37=makeQuery(id+"F3.imprint","IMPRINT",FACE,{"disambiguationData":[TD([[makeQuery(id+"F3.imprint","IMPRINT",EDGE,{"derivedFrom":sQuery(id+"F3.wireOp",EDGE,"E55")}),1.0]])]});
            var Q38;
            {var subQ0=sQuery(id+"F9.wireOp",EDGE,"E95");Q38=makeQuery(id+"F9.imprint","IMPRINT",FACE,{"disambiguationData":[TD([[makeQuery(id+"F9.imprint","IMPRINT",EDGE,{"derivedFrom":subQ0}),-1.0]])]});}
            var Q39;
            {var subQ0=sQuery(id+"F9.wireOp",EDGE,"E103");Q39=makeQuery(id+"F9.imprint","IMPRINT",FACE,{"disambiguationData":[TD([[makeQuery(id+"F9.imprint","IMPRINT",EDGE,{"derivedFrom":subQ0}),-1.0]])]});}
            var Q40;
            {var subQ0=sQuery(id+"F9.wireOp",EDGE,"E114");Q40=makeQuery(id+"F9.imprint","IMPRINT",FACE,{"disambiguationData":[TD([[makeQuery(id+"F9.imprint","IMPRINT",EDGE,{"derivedFrom":subQ0}),-1.0]])]});}
            var Q41;
            {var subQ0=sQuery(id+"F9.wireOp",EDGE,"E89");Q41=makeQuery(id+"F9.imprint","IMPRINT",FACE,{"disambiguationData":[TD([[makeQuery(id+"F9.imprint","IMPRINT",EDGE,{"derivedFrom":subQ0}),1.0]])]});}
            var Q42;
            Q42=makeQuery(id+"F10.imprint","IMPRINT",FACE,{"disambiguationData":[TD([[makeQuery(id+"F10.imprint","IMPRINT",EDGE,{"derivedFrom":sQuery(id+"F10.wireOp",EDGE,"E121")}),-1.0]])]});
            var Q43;
            Q43=makeQuery(id+"F3.imprint","IMPRINT",FACE,{"disambiguationData":[TD([[makeQuery(id+"F3.imprint","IMPRINT",EDGE,{"derivedFrom":sQuery(id+"F3.wireOp",EDGE,"E54")}),1.0]])]});
            var Q44;
            Q44=makeQuery(id+"F3.imprint","IMPRINT",FACE,{"disambiguationData":[TD([[makeQuery(id+"F3.imprint","IMPRINT",EDGE,{"derivedFrom":sQuery(id+"F3.wireOp",EDGE,"E52")}),1.0]])]});
            var Q45;
            Q45=makeQuery(id+"F3.imprint","IMPRINT",FACE,{"disambiguationData":[TD([[makeQuery(id+"F3.imprint","IMPRINT",EDGE,{"derivedFrom":sQuery(id+"F3.wireOp",EDGE,"E39")}),1.0]])]});
            var Q46;
            Q46=makeQuery(id+"F3.imprint","IMPRINT",FACE,{"disambiguationData":[TD([[makeQuery(id+"F3.imprint","IMPRINT",EDGE,{"derivedFrom":sQuery(id+"F3.wireOp",EDGE,"E40")}),1.0]])]});
            var Q47;
            Q47=makeQuery(id+"F3.imprint","IMPRINT",FACE,{"disambiguationData":[TD([[makeQuery(id+"F3.imprint","IMPRINT",EDGE,{"derivedFrom":sQuery(id+"F3.wireOp",EDGE,"E41")}),1.0]])]});
            var Q48;
            Q48=makeQuery(id+"F3.imprint","IMPRINT",FACE,{"disambiguationData":[TD([[makeQuery(id+"F3.imprint","IMPRINT",EDGE,{"derivedFrom":sQuery(id+"F3.wireOp",EDGE,"E42")}),1.0]])]});
            var Q49;
            Q49=makeQuery(id+"F3.imprint","IMPRINT",FACE,{"disambiguationData":[TD([[makeQuery(id+"F3.imprint","IMPRINT",EDGE,{"derivedFrom":sQuery(id+"F3.wireOp",EDGE,"E43")}),1.0]])]});
            var Q50;
            Q50=makeQuery(id+"F3.imprint","IMPRINT",FACE,{"disambiguationData":[TD([[makeQuery(id+"F3.imprint","IMPRINT",EDGE,{"derivedFrom":sQuery(id+"F3.wireOp",EDGE,"E44")}),1.0]])]});
            var Q51;
            Q51=makeQuery(id+"F3.imprint","IMPRINT",FACE,{"disambiguationData":[TD([[makeQuery(id+"F3.imprint","IMPRINT",EDGE,{"derivedFrom":sQuery(id+"F3.wireOp",EDGE,"E45")}),1.0]])]});
            var Q52;
            Q52=makeQuery(id+"F3.imprint","IMPRINT",FACE,{"disambiguationData":[TD([[makeQuery(id+"F3.imprint","IMPRINT",EDGE,{"derivedFrom":sQuery(id+"F3.wireOp",EDGE,"E46")}),1.0]])]});
            var Q53;
            Q53=makeQuery(id+"F3.imprint","IMPRINT",FACE,{"disambiguationData":[TD([[makeQuery(id+"F3.imprint","IMPRINT",EDGE,{"derivedFrom":sQuery(id+"F3.wireOp",EDGE,"E49")}),1.0]])]});
            var Q54;
            Q54=makeQuery(id+"F3.imprint","IMPRINT",FACE,{"disambiguationData":[TD([[makeQuery(id+"F3.imprint","IMPRINT",EDGE,{"derivedFrom":sQuery(id+"F3.wireOp",EDGE,"E50")}),1.0]])]});
            var Q55;
            Q55=makeQuery(id+"F3.imprint","IMPRINT",FACE,{"disambiguationData":[TD([[makeQuery(id+"F3.imprint","IMPRINT",EDGE,{"derivedFrom":sQuery(id+"F3.wireOp",EDGE,"E51")}),1.0]])]});
            var Q56;
            {var subQ1=sQuery(id+"F10.wireOp",EDGE,"E119");Q56=makeQuery(id+"F10.imprint","IMPRINT",FACE,{"disambiguationData":[TD([[makeQuery(id+"F10.imprint","IMPRINT",EDGE,{"derivedFrom":subQ1}),-1.0]])]});}
            var Q57;
            Q57=makeQuery(id+"F10.imprint","IMPRINT",FACE,{"disambiguationData":[TD([[makeQuery(id+"F10.imprint","IMPRINT",EDGE,{"derivedFrom":sQuery(id+"F10.wireOp",EDGE,"E131")}),-1.0]])]});
            var Q58;
            {var subQ2=sQuery(id+"F10.wireOp",EDGE,"E118");Q58=makeQuery(id+"F10.imprint","IMPRINT",FACE,{"disambiguationData":[TD([[makeQuery(id+"F10.imprint","IMPRINT",EDGE,{"derivedFrom":subQ2}),1.0]])]});}
            var Q59;
            {var subQ0=sQuery(id+"F0.wireOp",EDGE,"E19");var subQ1=sQuery(id+"F0.wireOp",EDGE,"E18");var subQ2=makeQuery(id+"F0.imprint","INTERSECT",VERTEX,{"disambiguationData":[OD(0.0)],"derivedFrom":[subQ1,subQ0]});Q59=makeQuery(id+"F0.imprint","IMPRINT",FACE,{"disambiguationData":[TD([[makeQuery(id+"F0.imprint","IMPRINT",EDGE,{"disambiguationData":[TD([[subQ2,1.0]])],"derivedFrom":subQ1}),1.0]])]});}
            var Q60;
            {var subQ1=sQuery(id+"F10.wireOp",EDGE,"E118");Q60=makeQuery(id+"F10.imprint","IMPRINT",FACE,{"disambiguationData":[TD([[makeQuery(id+"F10.imprint","IMPRINT",EDGE,{"derivedFrom":subQ1}),-1.0]])]});}
            var Q61;
            {var subQ0=sQuery(id+"F10.wireOp",EDGE,"E151");Q61=makeQuery(id+"F10.imprint","IMPRINT",FACE,{"disambiguationData":[TD([[makeQuery(id+"F10.imprint","IMPRINT",EDGE,{"derivedFrom":subQ0}),1.0]])]});}
            var Q62;
            Q62=makeQuery(id+"F10.imprint","IMPRINT",FACE,{"disambiguationData":[TD([[makeQuery(id+"F10.imprint","IMPRINT",EDGE,{"derivedFrom":sQuery(id+"F10.wireOp",EDGE,"E131")}),1.0]])]});
            var Q63;
            {var subQ3=sQuery(id+"F10.wireOp",EDGE,"E128");Q63=makeQuery(id+"F10.imprint","IMPRINT",FACE,{"disambiguationData":[TD([[makeQuery(id+"F10.imprint","IMPRINT",EDGE,{"derivedFrom":subQ3}),-1.0]])]});}
            var Q64;
            {var subQ3=sQuery(id+"F10.wireOp",EDGE,"E151");Q64=makeQuery(id+"F10.imprint","IMPRINT",FACE,{"disambiguationData":[TD([[makeQuery(id+"F10.imprint","IMPRINT",EDGE,{"derivedFrom":subQ3}),-1.0]])]});}
            var Q65;
            Q65=makeQuery(id+"F10.imprint","IMPRINT",FACE,{"disambiguationData":[TD([[makeQuery(id+"F10.imprint","IMPRINT",EDGE,{"derivedFrom":sQuery(id+"F10.wireOp",EDGE,"E132")}),-1.0]])]});
            extrude(context, id + "F13", {"entities" : qUnion([Q0, Q1, Q2, Q3, Q4, Q5, Q6, Q7, Q8, Q9, Q10, Q11, Q12, Q13, Q14, Q15, Q16, Q17, Q18, Q19, Q20, Q21, Q22, Q23, Q24, Q25, Q26, Q27, Q28, Q29, Q30, Q31, Q32, Q33, Q34, Q35, Q36, Q37, Q38, Q39, Q40, Q41, Q42, Q43, Q44, Q45, Q46, Q47, Q48, Q49, Q50, Q51, Q52, Q53, Q54, Q55, Q56, Q57, Q58, Q59, Q60, Q61, Q62, Q63, Q64, Q65]), "depth" : 50.8 * mm});
        }
        {
            var Q0;
            Q0=makeQuery(id+"F13.opExtrude","CAP_FACE",FACE,{"disambiguationData":[OSD([sQuery(id+"F8.wireOp",EDGE,"E83"),sQuery(id+"F8.wireOp",EDGE,"E84"),sQuery(id+"F8.wireOp",EDGE,"E85"),sQuery(id+"F8.wireOp",EDGE,"E86")])],"isStart":false});
            var Q1;
            Q1=makeQuery(id+"F13.opExtrude","CAP_FACE",FACE,{"disambiguationData":[OSD([sQuery(id+"F8.wireOp",EDGE,"E81"),sQuery(id+"F8.wireOp",EDGE,"E82"),sQuery(id+"F8.wireOp",EDGE,"E88")])],"isStart":false});
            var Q2;
            Q2=makeQuery(id+"F13.opExtrude","CAP_FACE",FACE,{"disambiguationData":[OSD([sQuery(id+"F8.wireOp",EDGE,"E79"),sQuery(id+"F8.wireOp",EDGE,"E80"),sQuery(id+"F8.wireOp",EDGE,"E87")])],"isStart":false});
            extrude(context, id + "F14", {"entities" : qUnion([Q0, Q1, Q2]), "operationType" : NewBodyOperationType.REMOVE, "oppositeDirection" : true, "depth" : 12.7 * mm});
        }
    });
